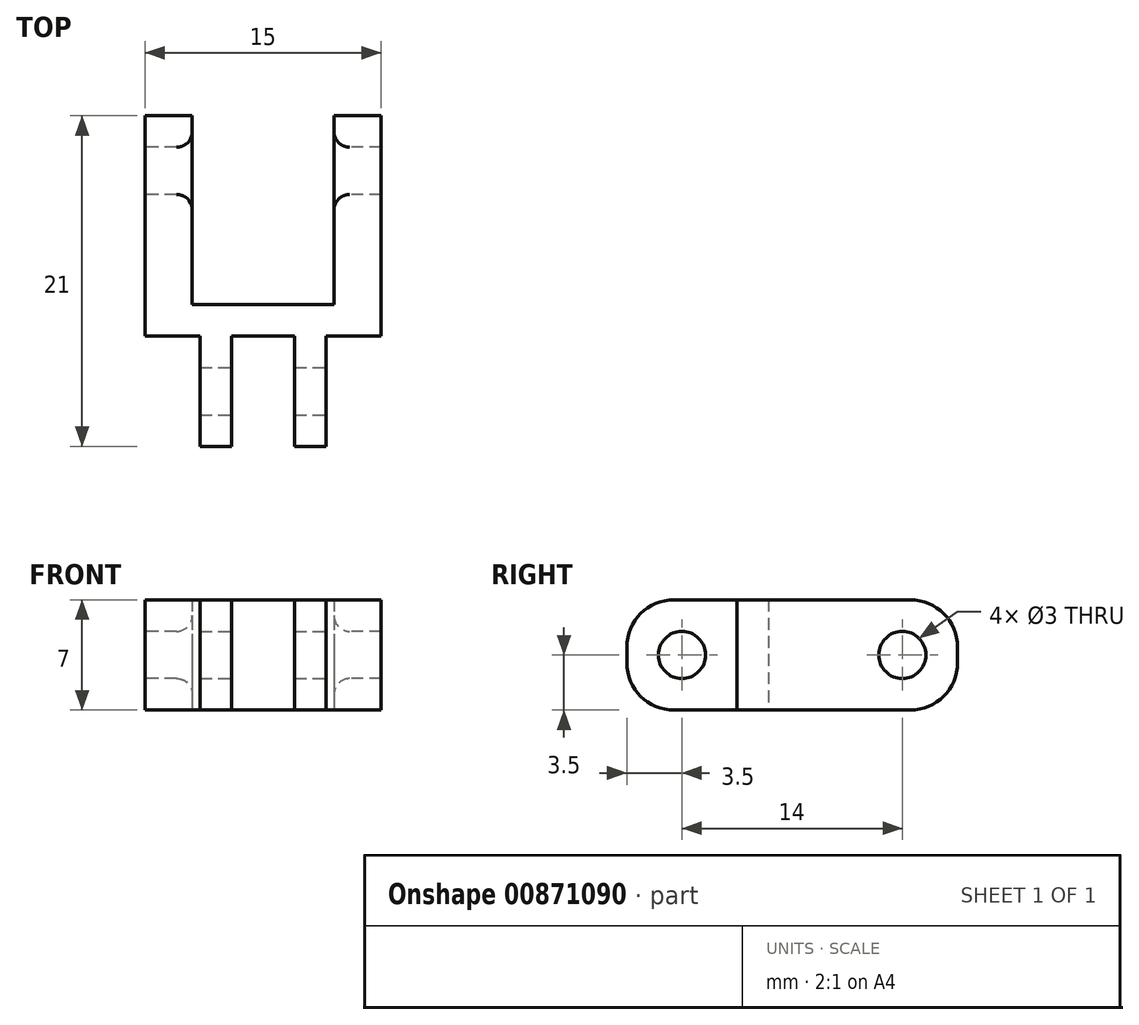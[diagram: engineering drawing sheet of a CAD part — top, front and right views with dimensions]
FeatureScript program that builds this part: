
annotation { "Feature Type Name" : "Feature", "Feature Type Description" : "" }
export const myFeature = defineFeature(function(context is Context, id is Id, definition is map)
    precondition{}
    {
        {
            var Q0;
            Q0=qCreatedBy(makeId("Top.planeOp"),FACE);
            var sketch = newSketch(context, id + "F0", { "sketchPlane" : qUnion([Q0])});
            skLineSegment(sketch, "E0.bottom", {"start": v(7.5, -1) * mm, "end": v(-7.5, -1) * mm});
            skLineSegment(sketch, "E0.top", {"start": v(7.5, 1) * mm, "end": v(-7.5, 1) * mm});
            skLineSegment(sketch, "E0.left", {"start": v(7.5, -1) * mm, "end": v(7.5, 1) * mm});
            skLineSegment(sketch, "E0.right", {"start": v(-7.5, -1) * mm, "end": v(-7.5, 1) * mm});
            skPoint(sketch, "E0.middle", {"position": v(0, 0) * mm});
            skLineSegment(sketch, "E1.bottom", {"start": v(-7.5, 1) * mm, "end": v(-4.5, 1) * mm});
            skLineSegment(sketch, "E1.top", {"start": v(-7.5, 13) * mm, "end": v(-4.5, 13) * mm});
            skLineSegment(sketch, "E1.left", {"start": v(-7.5, 1) * mm, "end": v(-7.5, 13) * mm});
            skLineSegment(sketch, "E1.right", {"start": v(-4.5, 1) * mm, "end": v(-4.5, 13) * mm});
            skLineSegment(sketch, "E2.bottom", {"start": v(-4, -1) * mm, "end": v(-2, -1) * mm});
            skLineSegment(sketch, "E2.top", {"start": v(-4, -8) * mm, "end": v(-2, -8) * mm});
            skLineSegment(sketch, "E2.left", {"start": v(-4, -1) * mm, "end": v(-4, -8) * mm});
            skLineSegment(sketch, "E2.right", {"start": v(-2, -1) * mm, "end": v(-2, -8) * mm});
            skLineSegment(sketch, "E3.MirrorCS", {"start": v(4, -1) * mm, "end": v(2, -1) * mm});
            skLineSegment(sketch, "E4.MirrorCS", {"start": v(7.5, 1) * mm, "end": v(4.5, 1) * mm});
            skLineSegment(sketch, "E5.MirrorCS", {"start": v(4, -1) * mm, "end": v(4, -8) * mm});
            skLineSegment(sketch, "E6.MirrorCS", {"start": v(4.5, 1) * mm, "end": v(4.5, 13) * mm});
            skLineSegment(sketch, "E7.MirrorCS", {"start": v(7.5, 1) * mm, "end": v(7.5, 13) * mm});
            skLineSegment(sketch, "E8.MirrorCS", {"start": v(2, -1) * mm, "end": v(2, -8) * mm});
            skLineSegment(sketch, "E9.MirrorCS", {"start": v(4, -8) * mm, "end": v(2, -8) * mm});
            skLineSegment(sketch, "E10.MirrorCS", {"start": v(7.5, 13) * mm, "end": v(4.5, 13) * mm});
            skSolve(sketch);
        }
        {
            var Q0;
            Q0=makeQuery(id+"F0.imprint","IMPRINT",FACE,{"disambiguationData":[TD([[makeQuery(id+"F0.imprint","IMPRINT",EDGE,{"derivedFrom":sQuery(id+"F0.wireOp",EDGE,"E2.top")}),1.0]])]});
            var Q1;
            Q1=makeQuery(id+"F0.imprint","IMPRINT",FACE,{"disambiguationData":[TD([[makeQuery(id+"F0.imprint","IMPRINT",EDGE,{"derivedFrom":sQuery(id+"F0.wireOp",EDGE,"E1.top")}),-1.0]])]});
            var Q2;
            {var subQ0=sQuery(id+"F0.wireOp",EDGE,"E6.MirrorCS");Q2=makeQuery(id+"F0.imprint","IMPRINT",FACE,{"disambiguationData":[TD([[makeQuery(id+"F0.imprint","IMPRINT",EDGE,{"derivedFrom":subQ0}),-1.0]])]});}
            var Q3;
            {var subQ5=sQuery(id+"F0.wireOp",EDGE,"E0.left");Q3=makeQuery(id+"F0.imprint","IMPRINT",FACE,{"disambiguationData":[TD([[makeQuery(id+"F0.imprint","IMPRINT",EDGE,{"derivedFrom":subQ5}),1.0]])]});}
            var Q4;
            {var subQ2=sQuery(id+"F0.wireOp",EDGE,"E5.MirrorCS");Q4=makeQuery(id+"F0.imprint","IMPRINT",FACE,{"disambiguationData":[TD([[makeQuery(id+"F0.imprint","IMPRINT",EDGE,{"derivedFrom":subQ2}),-1.0]])]});}
            extrude(context, id + "F1", {"entities" : qUnion([Q0, Q1, Q2, Q3, Q4]), "depth" : 7 * mm, "offsetDistance" : 25 * mm});
        }
        {
            var Q0;
            Q0=makeQuery(id+"F1.opExtrude","SWEPT_FACE",FACE,{"disambiguationData":[OSD([sQuery(id+"F0.wireOp",EDGE,"E5.MirrorCS")])]});
            var sketch = newSketch(context, id + "F2", { "sketchPlane" : qUnion([Q0])});
            skLineSegment(sketch, "E11", {"start": v(-4.5, 7) * mm, "end": v(-4.5, 1.86) * mm, "construction": true});
            skLineSegment(sketch, "E12", {"start": v(-8, 3.5) * mm, "end": v(-3.42, 3.5) * mm, "construction": true});
            skCircle(sketch, "E13", {"center": v(-4.5, 3.5) * mm, "radius": 1.5 * mm});
            skSolve(sketch);
        }
        {
            var Q0;
            Q0=makeQuery(id+"F2.imprint","IMPRINT",FACE,{"disambiguationData":[TD([[makeQuery(id+"F2.imprint","IMPRINT",EDGE,{"derivedFrom":sQuery(id+"F2.wireOp",EDGE,"E13")}),1.0]])]});
            extrude(context, id + "F3", {"entities" : qUnion([Q0]), "operationType" : NewBodyOperationType.REMOVE, "oppositeDirection" : true, "depth" : 12 * mm, "offsetDistance" : 25 * mm});
        }
        {
            var Q0;
            Q0=makeQuery(id+"F1.opExtrude","CAP_EDGE",EDGE,{"disambiguationData":[OSD([sQuery(id+"F0.wireOp",EDGE,"E2.top")])],"isStart":true});
            var Q1;
            Q1=makeQuery(id+"F1.opExtrude","CAP_EDGE",EDGE,{"disambiguationData":[OSD([sQuery(id+"F0.wireOp",EDGE,"E9.MirrorCS")])],"isStart":true});
            var Q2;
            Q2=makeQuery(id+"F1.opExtrude","CAP_EDGE",EDGE,{"disambiguationData":[OSD([sQuery(id+"F0.wireOp",EDGE,"E9.MirrorCS")])],"isStart":false});
            var Q3;
            Q3=makeQuery(id+"F1.opExtrude","CAP_EDGE",EDGE,{"disambiguationData":[OSD([sQuery(id+"F0.wireOp",EDGE,"E2.top")])],"isStart":false});
            var Q4;
            Q4=makeQuery(id+"F1.opExtrude","CAP_EDGE",EDGE,{"disambiguationData":[OSD([sQuery(id+"F0.wireOp",EDGE,"E1.top")])],"isStart":true});
            var Q5;
            Q5=makeQuery(id+"F1.opExtrude","CAP_EDGE",EDGE,{"disambiguationData":[OSD([sQuery(id+"F0.wireOp",EDGE,"E10.MirrorCS")])],"isStart":true});
            var Q6;
            Q6=makeQuery(id+"F1.opExtrude","CAP_EDGE",EDGE,{"disambiguationData":[OSD([sQuery(id+"F0.wireOp",EDGE,"E1.top")])],"isStart":false});
            var Q7;
            Q7=makeQuery(id+"F1.opExtrude","CAP_EDGE",EDGE,{"disambiguationData":[OSD([sQuery(id+"F0.wireOp",EDGE,"E10.MirrorCS")])],"isStart":false});
            fillet(context, id + "F4", {"entities" : qUnion([Q0, Q1, Q2, Q3, Q4, Q5, Q6, Q7]), "radius" : 3 * mm, "tangentPropagation" : true, "allowEdgeOverflow" : false});
        }
        {
            var Q0;
            Q0=makeQuery(id+"F1.opExtrude","SWEPT_FACE",FACE,{"disambiguationData":[OSD([sQuery(id+"F0.wireOp",EDGE,"E0.right"),sQuery(id+"F0.wireOp",EDGE,"E1.left")])]});
            var sketch = newSketch(context, id + "F5", { "sketchPlane" : qUnion([Q0])});
            skLineSegment(sketch, "E14", {"start": v(1, 3.5) * mm, "end": v(-15.17, 3.5) * mm, "construction": true});
            skPoint(sketch, "E15", {"position": v(-9.5, 3.5) * mm});
            skCircle(sketch, "E16", {"center": v(-9.5, 3.5) * mm, "radius": 1.5 * mm});
            skSolve(sketch);
        }
        {
            var Q0;
            Q0=makeQuery(id+"F5.imprint","IMPRINT",FACE,{"disambiguationData":[TD([[makeQuery(id+"F5.imprint","IMPRINT",EDGE,{"derivedFrom":sQuery(id+"F5.wireOp",EDGE,"E16")}),1.0]])]});
            extrude(context, id + "F6", {"entities" : qUnion([Q0]), "operationType" : NewBodyOperationType.REMOVE, "oppositeDirection" : true, "depth" : 25 * mm, "offsetDistance" : 25 * mm});
        }
        {
            var Q0;
            Q0=makeQuery(id+"F6.boolean.opBoolean","INTERSECT",EDGE,{"derivedFrom":[makeQuery(id+"F1.opExtrude","SWEPT_FACE",FACE,{"disambiguationData":[OSD([sQuery(id+"F0.wireOp",EDGE,"E6.MirrorCS")])]}),makeQuery(id+"F6.opExtrude","SWEPT_FACE",FACE,{"disambiguationData":[OSD([sQuery(id+"F5.wireOp",EDGE,"E16")])]})]});
            var Q1;
            Q1=makeQuery(id+"F6.boolean.opBoolean","INTERSECT",EDGE,{"derivedFrom":[makeQuery(id+"F1.opExtrude","SWEPT_FACE",FACE,{"disambiguationData":[OSD([sQuery(id+"F0.wireOp",EDGE,"E1.right")])]}),makeQuery(id+"F6.opExtrude","SWEPT_FACE",FACE,{"disambiguationData":[OSD([sQuery(id+"F5.wireOp",EDGE,"E16")])]})]});
            fillet(context, id + "F7", {"entities" : qUnion([Q0, Q1]), "radius" : 1 * mm, "tangentPropagation" : true, "allowEdgeOverflow" : false});
        }
    });
